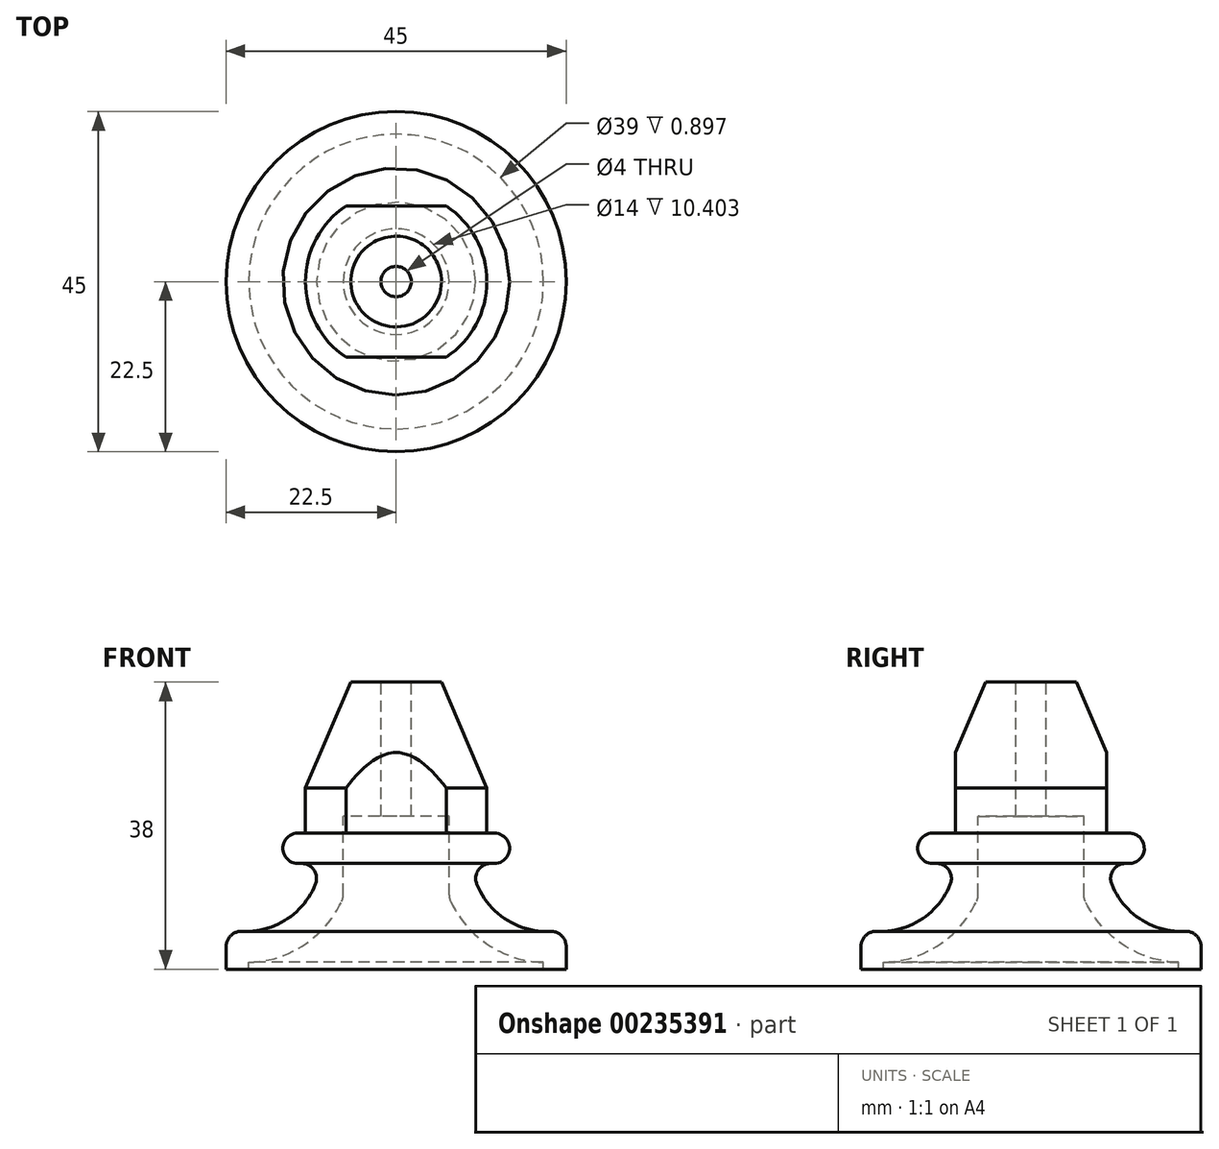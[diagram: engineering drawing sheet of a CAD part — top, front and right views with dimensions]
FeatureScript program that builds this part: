
annotation { "Feature Type Name" : "Feature", "Feature Type Description" : "" }
export const myFeature = defineFeature(function(context is Context, id is Id, definition is map)
    precondition{}
    {
        {
            var Q0;
            Q0=qCreatedBy(makeId("Right.planeOp"),FACE);
            var sketch = newSketch(context, id + "F0", { "sketchPlane" : qUnion([Q0])});
            skLineSegment(sketch, "E0", {"start": v(0, 0) * mm, "end": v(10, 0) * mm});
            skLineSegment(sketch, "E1", {"start": v(22.5, 0) * mm, "end": v(22.5, 3) * mm});
            skLineSegment(sketch, "E2", {"start": v(15, 18) * mm, "end": v(15, 18) * mm});
            skLineSegment(sketch, "E3", {"start": v(6, 38) * mm, "end": v(2, 38) * mm});
            skLineSegment(sketch, "E4", {"start": v(0, 38) * mm, "end": v(0, 0) * mm});
            skLineSegment(sketch, "E5", {"start": v(15, 16) * mm, "end": v(15, 16) * mm});
            skLineSegment(sketch, "E6", {"start": v(13, 14) * mm, "end": v(12.53, 14) * mm});
            skLineSegment(sketch, "E7", {"start": v(10, 33.87) * mm, "end": v(10, 33.33) * mm, "construction": true});
            skLineSegment(sketch, "E8", {"start": v(10, 14) * mm, "end": v(10, 5) * mm});
            skLineSegment(sketch, "E9.trimOffspring", {"start": v(10, 0) * mm, "end": v(10, -3.38) * mm, "construction": true});
            skArc(sketch, "E10", {"start": v(10.68, 11.25) * mm, "mid": v(14.55, 6.58) * mm, "end": v(20.4, 5) * mm});
            skPoint(sketch, "E11.visualSharp", {"position": v(22.5, 5.32) * mm});
            skArc(sketch, "E11.filletArc", {"start": v(22.5, 3) * mm, "mid": v(21.88, 4.45) * mm, "end": v(20.4, 5) * mm});
            skPoint(sketch, "E12.end.orphan", {"position": v(12, 31) * mm});
            skLineSegment(sketch, "E13", {"start": v(6, 38) * mm, "end": v(12, 24) * mm});
            skLineSegment(sketch, "E14", {"start": v(12, 24) * mm, "end": v(12, 18) * mm});
            skLineSegment(sketch, "E15", {"start": v(12, 18) * mm, "end": v(13, 18) * mm});
            skPoint(sketch, "E16.visualSharp", {"position": v(10, 14) * mm});
            skArc(sketch, "E16.filletArc", {"start": v(12.53, 14) * mm, "mid": v(10.87, 13.12) * mm, "end": v(10.68, 11.25) * mm});
            skLineSegment(sketch, "E17", {"start": v(2, 38) * mm, "end": v(2, 20.25) * mm});
            skPoint(sketch, "E18.end.orphan", {"position": v(6, 20.25) * mm});
            skLineSegment(sketch, "E19", {"start": v(2, 20.25) * mm, "end": v(7, 20.25) * mm});
            skLineSegment(sketch, "E20", {"start": v(7, 20.25) * mm, "end": v(7, 9.84) * mm});
            skLineSegment(sketch, "E21", {"start": v(0, 40.07) * mm, "end": v(0, -0.99) * mm, "construction": true});
            skArc(sketch, "E22.0", {"start": v(7.19, 9) * mm, "mid": v(12.2, 3.2) * mm, "end": v(19.5, 0.9) * mm});
            skLineSegment(sketch, "E23", {"start": v(19.5, 0.9) * mm, "end": v(19.5, 0) * mm});
            skPoint(sketch, "E24.end.orphan", {"position": v(20.6, 0) * mm});
            skPoint(sketch, "E25.visualSharp", {"position": v(15, 18) * mm});
            skArc(sketch, "E25.filletArc", {"start": v(15, 16) * mm, "mid": v(14.41, 17.41) * mm, "end": v(13, 18) * mm});
            skPoint(sketch, "E26.visualSharp", {"position": v(15, 14) * mm});
            skArc(sketch, "E26.filletArc", {"start": v(13, 14) * mm, "mid": v(14.41, 14.59) * mm, "end": v(15, 16) * mm});
            skPoint(sketch, "E27.newPointA", {"position": v(7, 0) * mm});
            skArc(sketch, "E27.filletArc", {"start": v(7, 9.84) * mm, "mid": v(7.05, 9.4) * mm, "end": v(7.19, 9) * mm});
            skLineSegment(sketch, "E28.trimOffspring", {"start": v(19.5, 0) * mm, "end": v(22.5, 0) * mm});
            skSolve(sketch);
        }
        {
            var Q0;
            Q0=makeQuery(id+"F0.imprint","IMPRINT",FACE,{"disambiguationData":[TD([[makeQuery(id+"F0.imprint","IMPRINT",EDGE,{"derivedFrom":sQuery(id+"F0.wireOp",EDGE,"E1")}),1.0]])]});
            var Q1;
            Q1=sQuery(id+"F0.wireOp",EDGE,"E4");
            revolve(context, id + "F1", {"entities" : qUnion([Q0]), "axis" : qUnion([Q1]), "revolveType" : RevolveType.FULL});
        }
        {
            var Q0;
            Q0=makeQuery(id+"F1.opRevolve","SWEPT_FACE",FACE,{"disambiguationData":[OSD([sQuery(id+"F0.wireOp",EDGE,"E3")])]});
            var sketch = newSketch(context, id + "F2", { "sketchPlane" : qUnion([Q0])});
            skCircle(sketch, "E29.0", {"center": v(0, 0) * mm, "radius": 12 * mm});
            skCircle(sketch, "E30.0", {"center": v(0, 0) * mm, "radius": 6 * mm});
            skLineSegment(sketch, "E31.bottom", {"start": v(6.63, -10) * mm, "end": v(-6.63, -10) * mm});
            skLineSegment(sketch, "E31.top", {"start": v(6.63, 10) * mm, "end": v(-6.63, 10) * mm});
            skLineSegment(sketch, "E31.left", {"start": v(6.63, -10) * mm, "end": v(6.63, 10) * mm});
            skLineSegment(sketch, "E31.right", {"start": v(-6.63, -10) * mm, "end": v(-6.63, 10) * mm});
            skSolve(sketch);
        }
        {
            var Q0;
            {var subQ0=sQuery(id+"F2.wireOp",EDGE,"E31.top");Q0=makeQuery(id+"F2.imprint","IMPRINT",FACE,{"disambiguationData":[TD([[makeQuery(id+"F2.imprint","IMPRINT",EDGE,{"derivedFrom":subQ0}),-1.0]])]});}
            var Q1;
            {var subQ0=sQuery(id+"F2.wireOp",EDGE,"E31.bottom");Q1=makeQuery(id+"F2.imprint","IMPRINT",FACE,{"disambiguationData":[TD([[makeQuery(id+"F2.imprint","IMPRINT",EDGE,{"derivedFrom":subQ0}),1.0]])]});}
            var Q2;
            Q2=makeQuery(id+"F1.opRevolve","SWEPT_FACE",FACE,{"disambiguationData":[OSD([sQuery(id+"F0.wireOp",EDGE,"E15")])]});
            extrude(context, id + "F3", {"entities" : qUnion([Q0, Q1]), "operationType" : NewBodyOperationType.REMOVE, "endBound" : BoundingType.UP_TO_SURFACE, "oppositeDirection" : true, "endBoundEntityFace" : qUnion([Q2]), "depth" : 19 * mm});
        }
    });
